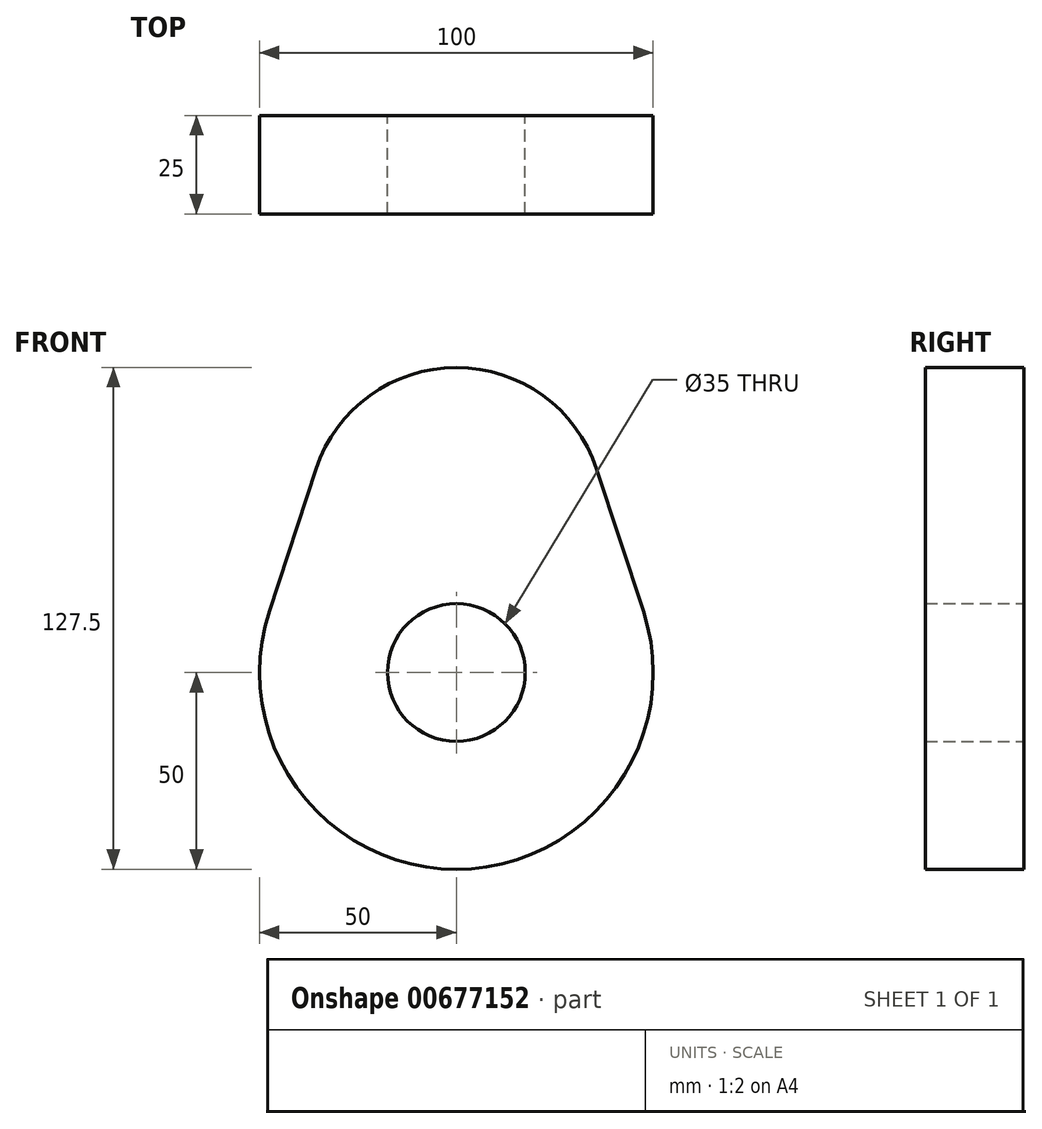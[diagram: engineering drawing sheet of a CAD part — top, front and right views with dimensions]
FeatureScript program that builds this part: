
annotation { "Feature Type Name" : "Feature", "Feature Type Description" : "" }
export const myFeature = defineFeature(function(context is Context, id is Id, definition is map)
    precondition{}
    {
        {
            var Q0;
            Q0=qCreatedBy(makeId("Front.planeOp"),FACE);
            var sketch = newSketch(context, id + "F0", { "sketchPlane" : qUnion([Q0])});
            skArc(sketch, "E0", {"start": v(35.62, 51.72) * mm, "mid": v(0, 77.5) * mm, "end": v(-35.62, 51.72) * mm});
            skLineSegment(sketch, "E1", {"start": v(47.5, 15.62) * mm, "end": v(35.62, 51.72) * mm});
            skLineSegment(sketch, "E2", {"start": v(-47.5, 15.63) * mm, "end": v(-35.62, 51.72) * mm});
            skArc(sketch, "E3.trimOffspring", {"start": v(-47.5, 15.62) * mm, "mid": v(0, -50) * mm, "end": v(47.5, 15.63) * mm});
            skCircle(sketch, "E4", {"center": v(0, 0) * mm, "radius": 17.5 * mm});
            skSolve(sketch);
        }
        {
            var Q0;
            Q0=makeQuery(id+"F0.imprint","IMPRINT",FACE,{"disambiguationData":[TD([[makeQuery(id+"F0.imprint","IMPRINT",EDGE,{"derivedFrom":sQuery(id+"F0.wireOp",EDGE,"E0")}),1.0]])]});
            extrude(context, id + "F1", {"entities" : qUnion([Q0]), "depth" : 25 * mm, "offsetDistance" : 25 * mm});
        }
    });
